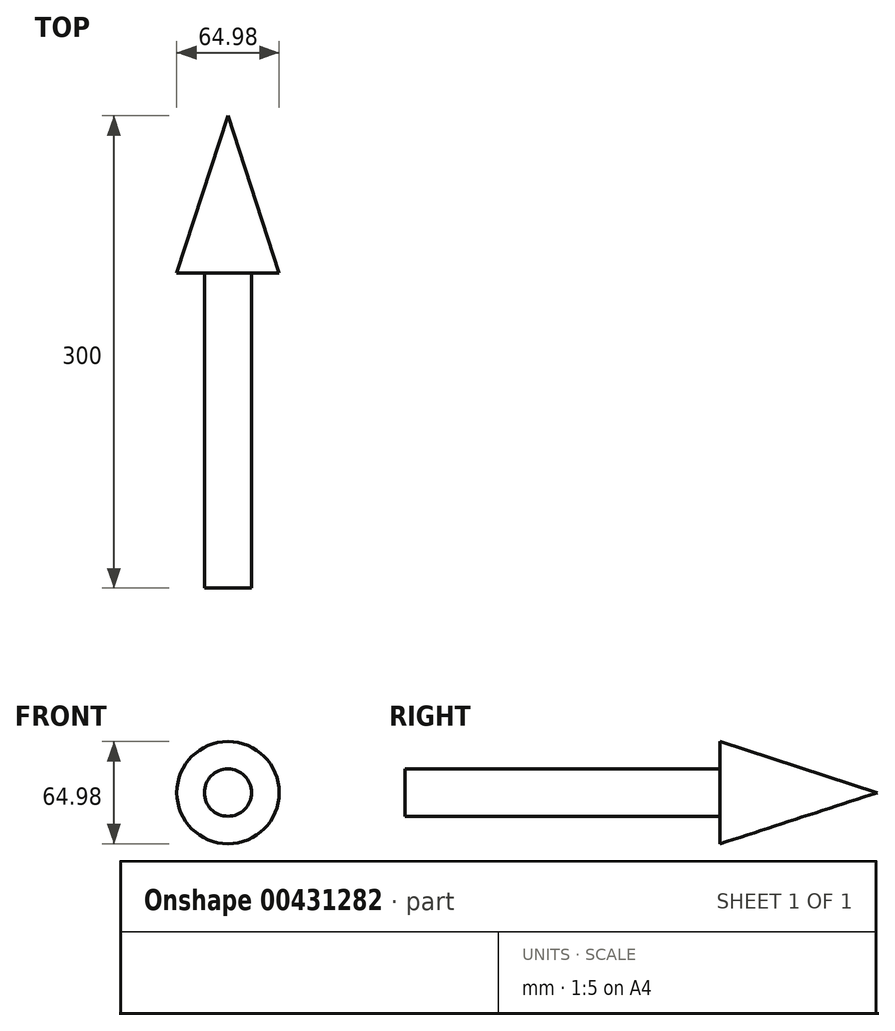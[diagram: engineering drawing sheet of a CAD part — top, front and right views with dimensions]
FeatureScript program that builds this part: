
annotation { "Feature Type Name" : "Feature", "Feature Type Description" : "" }
export const myFeature = defineFeature(function(context is Context, id is Id, definition is map)
    precondition{}
    {
        {
            var Q0;
            Q0=qCreatedBy(makeId("Right.planeOp"),FACE);
            var sketch = newSketch(context, id + "F0", { "sketchPlane" : qUnion([Q0])});
            skLineSegment(sketch, "E0", {"start": v(-105.84, 15) * mm, "end": v(94.16, 15) * mm});
            skLineSegment(sketch, "E1", {"start": v(94.16, 15) * mm, "end": v(94.16, 32.5) * mm});
            skLineSegment(sketch, "E2", {"start": v(94.16, 32.5) * mm, "end": v(194.16, 0) * mm});
            skLineSegment(sketch, "E3", {"start": v(194.16, 0) * mm, "end": v(-105.84, 0) * mm});
            skLineSegment(sketch, "E4", {"start": v(-105.84, 0) * mm, "end": v(-105.84, 15) * mm});
            skSolve(sketch);
        }
        {
            var Q0;
            Q0=makeQuery(id+"F0.imprint","IMPRINT",FACE,{"disambiguationData":[TD([[makeQuery(id+"F0.imprint","IMPRINT",EDGE,{"derivedFrom":sQuery(id+"F0.wireOp",EDGE,"E0")}),-1.0]])]});
            var Q1;
            Q1=sQuery(id+"F0.wireOp",EDGE,"E3");
            revolve(context, id + "F1", {"entities" : qUnion([Q0]), "axis" : qUnion([Q1]), "revolveType" : RevolveType.FULL});
        }
    });
